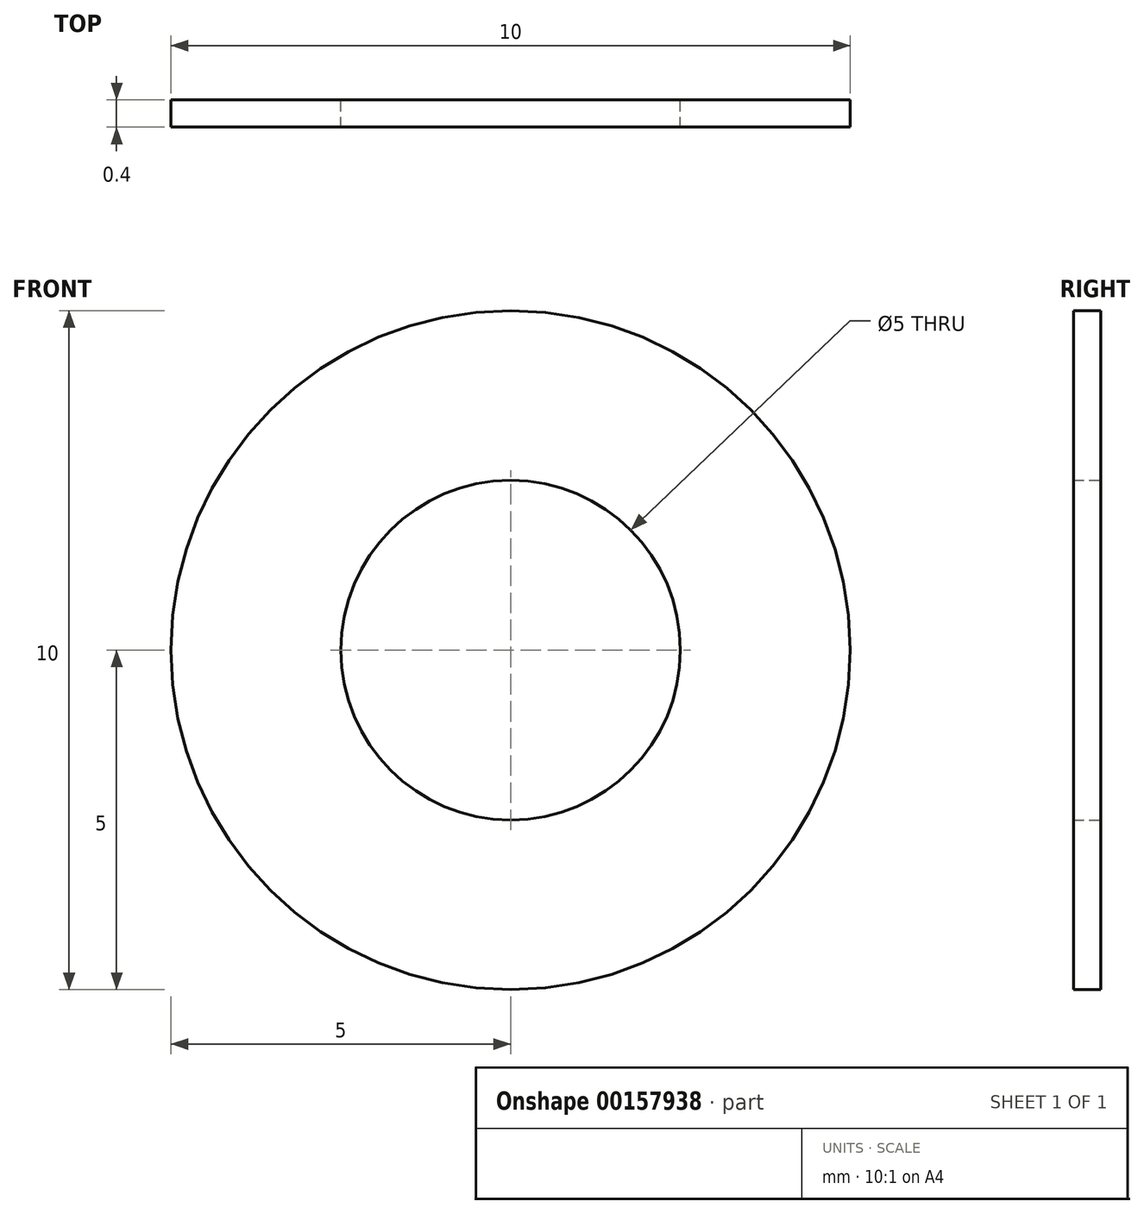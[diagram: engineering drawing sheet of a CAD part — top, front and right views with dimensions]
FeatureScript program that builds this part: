
annotation { "Feature Type Name" : "Feature", "Feature Type Description" : "" }
export const myFeature = defineFeature(function(context is Context, id is Id, definition is map)
    precondition{}
    {
        {
            assignVariable(context, id + "F0", {"name" : "h", "anyValue" : 0.4});
        }
        {
            var Q0;
            Q0=qCreatedBy(makeId("Front.planeOp"),FACE);
            var sketch = newSketch(context, id + "F1", { "sketchPlane" : qUnion([Q0])});
            skCircle(sketch, "E0", {"center": v(0, 0) * mm, "radius": 5 * mm});
            skCircle(sketch, "E1", {"center": v(0, 0) * mm, "radius": 2.5 * mm});
            skSolve(sketch);
        }
        {
            var Q0;
            Q0=makeQuery(id+"F1.imprint","IMPRINT",FACE,{"disambiguationData":[TD([[makeQuery(id+"F1.imprint","IMPRINT",EDGE,{"derivedFrom":sQuery(id+"F1.wireOp",EDGE,"E0")}),1.0]])]});
            extrude(context, id + "F2", {"entities" : qUnion([Q0]), "endBound" : BoundingType.SYMMETRIC, "depth" : (getVariable(context, 'h')) * mm});
        }
    });
